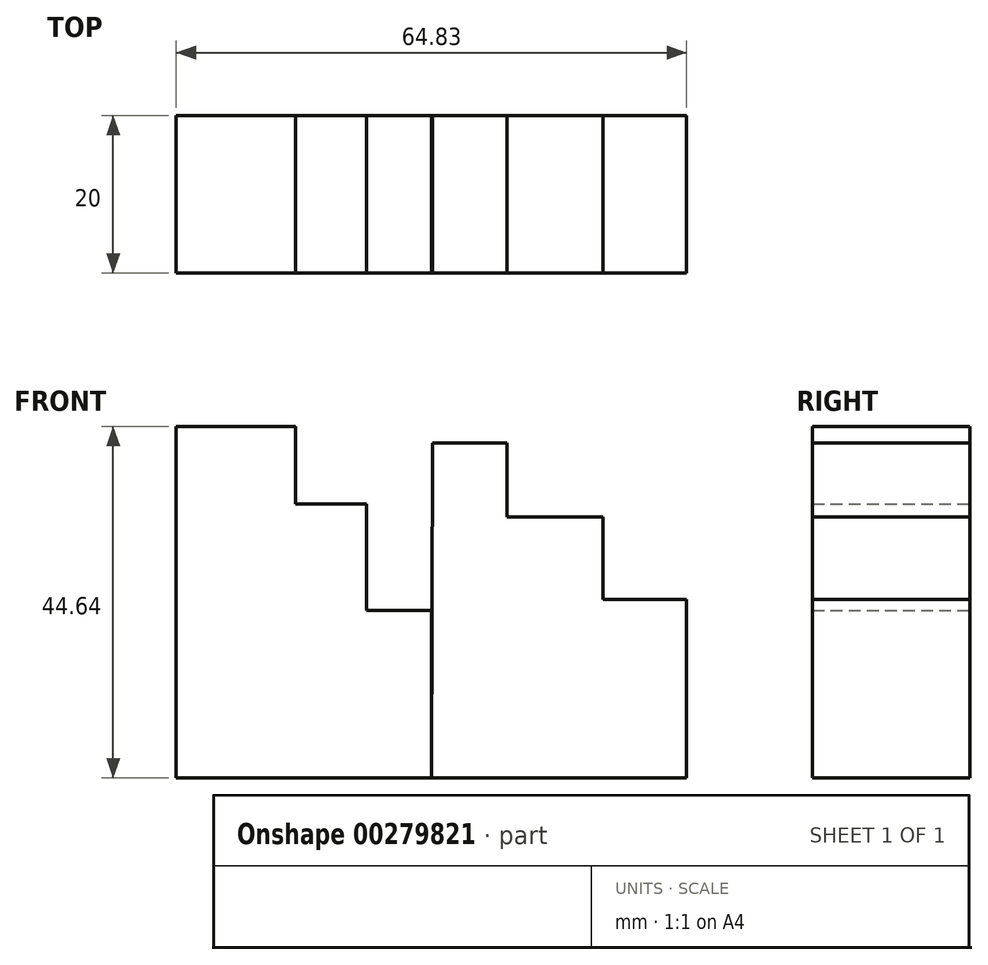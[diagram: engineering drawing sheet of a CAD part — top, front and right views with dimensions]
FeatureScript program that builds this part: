
annotation { "Feature Type Name" : "Feature", "Feature Type Description" : "" }
export const myFeature = defineFeature(function(context is Context, id is Id, definition is map)
    precondition{}
    {
        {
            var Q0;
            Q0=qCreatedBy(makeId("Front.planeOp"),FACE);
            var sketch = newSketch(context, id + "F0", { "sketchPlane" : qUnion([Q0])});
            skLineSegment(sketch, "E0", {"start": v(0, 0) * mm, "end": v(64.83, 0) * mm});
            skLineSegment(sketch, "E1", {"start": v(64.83, 0) * mm, "end": v(64.83, 22.69) * mm});
            skLineSegment(sketch, "E2", {"start": v(64.83, 22.69) * mm, "end": v(54.22, 22.69) * mm});
            skLineSegment(sketch, "E3", {"start": v(54.22, 22.69) * mm, "end": v(54.22, 0) * mm});
            skLineSegment(sketch, "E4", {"start": v(54.22, 0) * mm, "end": v(54.22, 33.15) * mm});
            skLineSegment(sketch, "E5", {"start": v(54.22, 33.15) * mm, "end": v(41.99, 33.15) * mm});
            skLineSegment(sketch, "E6", {"start": v(41.99, 33.15) * mm, "end": v(41.99, 0) * mm});
            skLineSegment(sketch, "E7", {"start": v(41.99, 0) * mm, "end": v(41.99, 33.15) * mm});
            skLineSegment(sketch, "E8", {"start": v(41.99, 33.15) * mm, "end": v(41.99, 42.58) * mm});
            skLineSegment(sketch, "E9", {"start": v(41.99, 42.58) * mm, "end": v(32.56, 42.58) * mm});
            skLineSegment(sketch, "E10", {"start": v(32.56, 42.58) * mm, "end": v(32.41, 0) * mm});
            skLineSegment(sketch, "E11", {"start": v(32.41, 0) * mm, "end": v(32.41, 21.29) * mm});
            skPoint(sketch, "E11.endSnap0", {"position": v(32.49, 21.29) * mm});
            skLineSegment(sketch, "E12", {"start": v(32.41, 21.29) * mm, "end": v(24.16, 21.29) * mm});
            skLineSegment(sketch, "E13", {"start": v(24.16, 21.29) * mm, "end": v(24.16, 0) * mm});
            skLineSegment(sketch, "E14", {"start": v(24.16, 0) * mm, "end": v(24.16, 34.77) * mm});
            skLineSegment(sketch, "E15", {"start": v(24.16, 34.77) * mm, "end": v(15.18, 34.77) * mm});
            skLineSegment(sketch, "E16", {"start": v(15.18, 34.77) * mm, "end": v(15.18, 0) * mm});
            skLineSegment(sketch, "E17", {"start": v(15.18, 0) * mm, "end": v(15.18, 34.77) * mm});
            skLineSegment(sketch, "E18", {"start": v(15.18, 34.77) * mm, "end": v(15.18, 44.64) * mm});
            skLineSegment(sketch, "E19", {"start": v(15.18, 44.64) * mm, "end": v(0, 44.64) * mm});
            skLineSegment(sketch, "E20", {"start": v(0, 44.64) * mm, "end": v(0, 0) * mm});
            skSolve(sketch);
        }
        {
            var Q0;
            Q0 = qSketchRegion(id + "F0", true);
            extrude(context, id + "F1", {"entities" : qUnion([Q0]), "depth" : 20 * mm});
        }
    });
